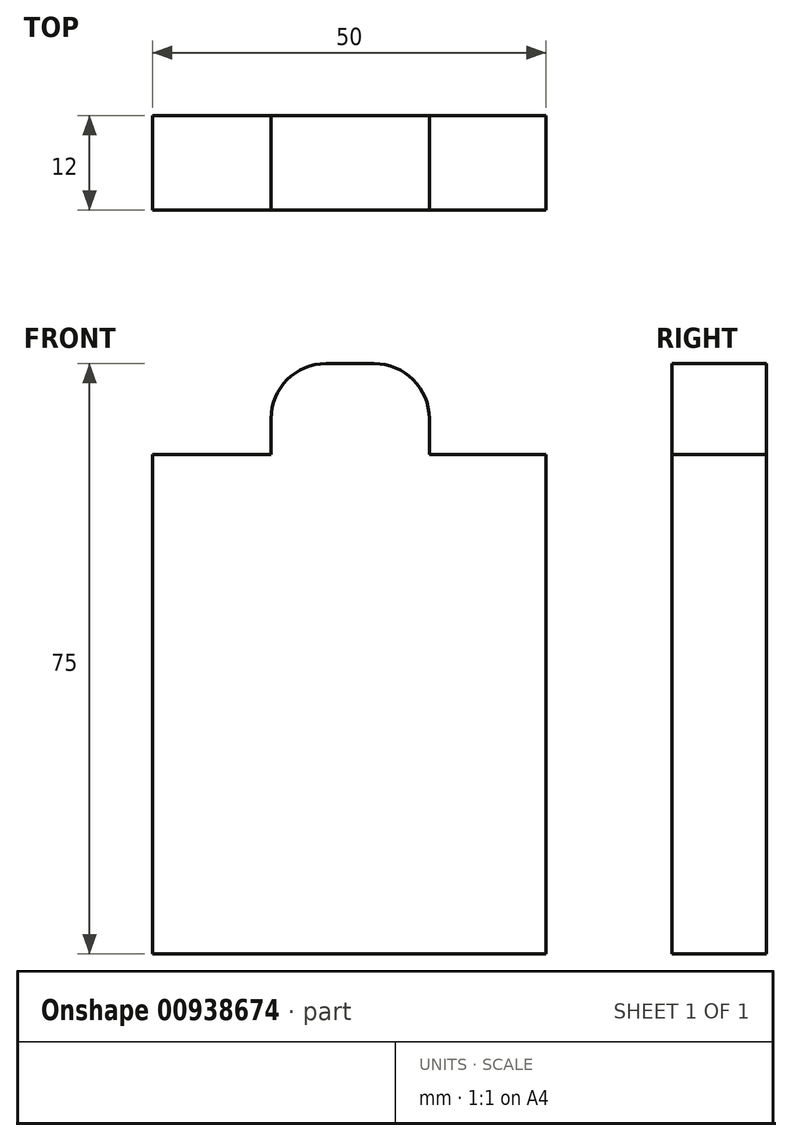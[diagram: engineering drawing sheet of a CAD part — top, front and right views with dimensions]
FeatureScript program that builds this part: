
annotation { "Feature Type Name" : "Feature", "Feature Type Description" : "" }
export const myFeature = defineFeature(function(context is Context, id is Id, definition is map)
    precondition{}
    {
        {
            var Q0;
            Q0=qCreatedBy(makeId("Front.planeOp"),FACE);
            var sketch = newSketch(context, id + "F0", { "sketchPlane" : qUnion([Q0])});
            skLineSegment(sketch, "E0.bottom", {"start": v(0, 0) * mm, "end": v(50, 0) * mm});
            skLineSegment(sketch, "E0.top", {"start": v(0, 75) * mm, "end": v(50, 75) * mm});
            skLineSegment(sketch, "E0.left", {"start": v(0, 0) * mm, "end": v(0, 75) * mm});
            skLineSegment(sketch, "E0.right", {"start": v(50, 0) * mm, "end": v(50, 75) * mm});
            skLineSegment(sketch, "E1.bottom", {"start": v(0, 75) * mm, "end": v(15.05, 75) * mm});
            skLineSegment(sketch, "E1.top", {"start": v(0, 63.43) * mm, "end": v(15.05, 63.43) * mm});
            skLineSegment(sketch, "E1.left", {"start": v(0, 75) * mm, "end": v(0, 63.43) * mm});
            skLineSegment(sketch, "E1.right", {"start": v(15.05, 75) * mm, "end": v(15.05, 63.43) * mm});
            skLineSegment(sketch, "E2.bottom", {"start": v(50, 75) * mm, "end": v(35.15, 75) * mm});
            skLineSegment(sketch, "E2.top", {"start": v(50, 63.43) * mm, "end": v(35.15, 63.43) * mm});
            skLineSegment(sketch, "E2.left", {"start": v(50, 75) * mm, "end": v(50, 63.43) * mm});
            skLineSegment(sketch, "E2.right", {"start": v(35.15, 75) * mm, "end": v(35.15, 63.43) * mm});
            skSolve(sketch);
        }
        {
            var Q0;
            Q0=makeQuery(id+"F0.imprint","IMPRINT",FACE,{"disambiguationData":[TD([[makeQuery(id+"F0.imprint","IMPRINT",EDGE,{"derivedFrom":sQuery(id+"F0.wireOp",EDGE,"E0.bottom")}),1.0]])]});
            extrude(context, id + "F1", {"entities" : qUnion([Q0]), "depth" : 12 * mm, "offsetDistance" : 25 * mm});
        }
        {
            var Q0;
            Q0=makeQuery(id+"F1.opExtrude","SWEPT_EDGE",EDGE,{"disambiguationData":[OSD([sQuery(id+"F0.wireOp",EDGE,"E0.top"),sQuery(id+"F0.wireOp",EDGE,"E2.bottom"),sQuery(id+"F0.wireOp",EDGE,"E2.right")])]});
            var Q1;
            Q1=makeQuery(id+"F1.opExtrude","SWEPT_EDGE",EDGE,{"disambiguationData":[OSD([sQuery(id+"F0.wireOp",EDGE,"E0.top"),sQuery(id+"F0.wireOp",EDGE,"E1.bottom"),sQuery(id+"F0.wireOp",EDGE,"E1.right")])]});
            fillet(context, id + "F2", {"entities" : qUnion([Q0, Q1]), "radius" : 7 * mm, "tangentPropagation" : true, "allowEdgeOverflow" : false});
        }
    });
